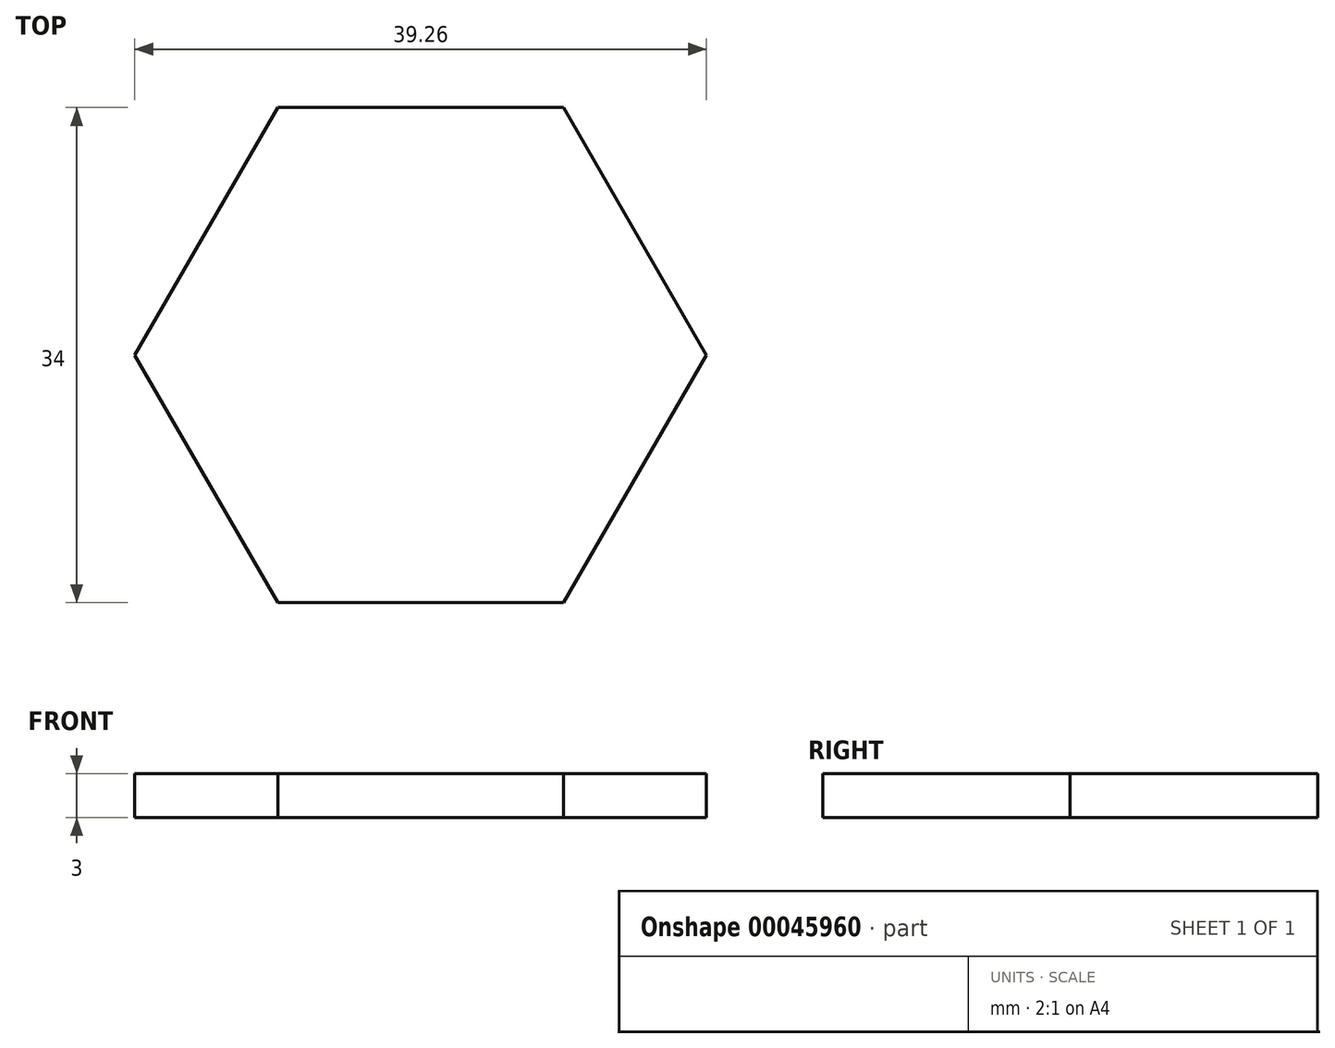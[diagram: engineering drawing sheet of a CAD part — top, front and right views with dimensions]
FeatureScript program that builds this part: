
annotation { "Feature Type Name" : "Feature", "Feature Type Description" : "" }
export const myFeature = defineFeature(function(context is Context, id is Id, definition is map)
    precondition{}
    {
        {
            var Q0;
            Q0=qCreatedBy(makeId("Top.planeOp"),FACE);
            var sketch = newSketch(context, id + "F0", { "sketchPlane" : qUnion([Q0])});
            skPoint(sketch, "E0.0.midPoint", {"position": v(0, -17) * mm});
            skCircle(sketch, "E0.cCircle", {"center": v(0, 0) * mm, "radius": 17 * mm, "construction": true});
            skLineSegment(sketch, "E0.0", {"start": v(9.81, -17) * mm, "end": v(-9.81, -17) * mm});
            skLineSegment(sketch, "E0.1", {"start": v(-9.81, -17) * mm, "end": v(-19.63, 0) * mm});
            skLineSegment(sketch, "E0.2", {"start": v(-19.63, 0) * mm, "end": v(-9.81, 17) * mm});
            skLineSegment(sketch, "E0.3", {"start": v(-9.81, 17) * mm, "end": v(9.81, 17) * mm});
            skLineSegment(sketch, "E0.4", {"start": v(9.81, 17) * mm, "end": v(19.63, 0) * mm});
            skLineSegment(sketch, "E0.5", {"start": v(19.63, 0) * mm, "end": v(9.81, -17) * mm});
            skSolve(sketch);
        }
        {
            var Q0;
            Q0 = qSketchRegion(id + "F0", true);
            extrude(context, id + "F1", {"entities" : qUnion([Q0]), "depth" : 3 * mm});
        }
    });
